# Revit family: NBS_ConceptCubicleSystems_PnlCbclSym_Curve
name_source: partatom
category: Specialty Equipment
units: mm (PartAtom-declared; Revit-internal decimal feet)

## family parameters
Always vertical = Yes
Cut with Voids When Loaded = No
Part Type = Normal
Room Calculation Point = No
Round Connector Dimension = Use Diameter
Shared = No
Work Plane-Based = No

## types (8) — shared parameters
AssetType = Fixed
Category = Ss_25_12_60_60:Panel cubicle systems
Description = Curve cubicles
DoorLeafMaterial = NBS_ConceptCubicleSystems_Z016_ZesteDeCitron-Yellow
DoorLeafUndercut = 150 mm
DurationUnit = year
Features = Black core with a radiused edge, back to back pull handle supplied with outward opening doors, non standard dimensions available on request, vandel and water resistant compact grade laminate
FittingMaterial = NBS_ConceptCubicleSystems_SatinAnodisedAluminium
Fittings = Powder coated aluminium with elliptical aluminium pilasters
IfcExportAs = IfcFurnitureType
IfcExportType = USERDEFINED
IsBuiltIn = Yes
ManufacturerName = Concept Cubicle Systems
ManufacturerURL = www.conceptcubiclesystems.co.uk
Material = Compact Grade Laminate
ModelReference = Curve Cubicles
NBSCertification = www.nationalbimlibrary.com/cert/b3h0bzth
NBSDescription = Panel cubicle system
NBSReference = 25-05-60/160
PanelSupports = 150 mm
PanelThickness = 13 mm
Panels = 12 mm Compact Grade Laminate
PartitionMaterial = NBS_ConceptCubicleSystems_Z016_ZesteDeCitron-Yellow
PartitionUndercut = 150 mm
PilasterMaterial = NBS_ConceptCubicleSystems_SatinAnodisedAluminium
ProductInformation = https://www.conceptcubiclesystems.co.uk
Size = 1500 x 1980 mm
Status = UNSET
Style = Cubicle
SystemManufacturer = Concept Cubicle Systems
Uniclass2015Code = Ss_25_12_60_60
Uniclass2015Title = Panel cubicle systems
Uniclass2015Version = Systems v1.17
Version = 3
WarrantyDurationUnit = year

## per-type parameters (varying)
| type | BIMObjectName | HasPartitionLeft | HasPartitionRight | HasPilasterLeftCorner | HasPilasterLeftWall | HasPilasterRight | HasPilasterRightCorner | HasPilasterRightWall | IsEndCubicle | IsFirstCubicle | IsMiddleCubicle | IsSingleCubicle | IsWallEndEndCubicle | IsWallEndFirstCubicle | IsWallEndSingleCubicle | IsWallToWallSingleCubicle | Name |
| SingleCubicle | NBS_ConceptCubicleSystems_PanelCubicleSystem_Curve_SingleCubicle | Yes | Yes | Yes | No | No | Yes | No | No | No | No | Yes | No | No | No | No | PanelCubicleSystem_Curve_SingleCubicle_ConceptCubicleSystems |
| WallToWallSingleCubicle | NBS_ConceptCubicleSystems_PanelCubicleSystem_Curve_WallToWallSingleCubicle | No | No | No | Yes | No | No | Yes | No | No | No | No | No | No | No | Yes | PanelCubicleSystem_Curve_WallToWallSingleCubicle_ConceptCubicleSystems |
| EndCubicle | NBS_ConceptCubicleSystems_PanelCubicleSystem_Curve_EndCubicle | No | Yes | No | No | No | Yes | No | Yes | No | No | No | No | No | No | No | PanelCubicleSystem_Curve_EndCubicle_ConceptCubicleSystems |
| FirstCubicle | NBS_ConceptCubicleSystems_PanelCubicleSystem_Curve_FirstCubicle | Yes | Yes | Yes | No | Yes | No | No | No | Yes | No | No | No | No | No | No | PanelCubicleSystem_Curve_FirstCubicle_ConceptCubicleSystems |
| WallEndFirstCubicle | NBS_ConceptCubicleSystems_PanelCubicleSystem_Curve_WallEndFirstCubicle | No | Yes | No | Yes | Yes | No | No | No | No | No | No | No | Yes | No | No | PanelCubicleSystem_Curve_WallEndFirstCubicle_ConceptCubicleSystems |
| WallEndSingleCubicle | NBS_ConceptCubicleSystems_PanelCubicleSystem_Curve_WallEndSingleCubicle | No | Yes | No | Yes | No | Yes | No | No | No | No | No | No | No | Yes | No | PanelCubicleSystem_Curve_WallEndSingleCubicle_ConceptCubicleSystems |
| MiddleCubicle | NBS_ConceptCubicleSystems_PanelCubicleSystem_Curve_MiddleCubicle | No | Yes | No | No | Yes | No | No | No | No | Yes | No | No | No | No | No | PanelCubicleSystem_Curve_MiddleCubicle_ConceptCubicleSystems |
| WallEndEndCubicle | NBS_ConceptCubicleSystems_PanelCubicleSystem_Curve_WallEndEndCubicle | No | No | No | No | No | No | Yes | No | No | No | No | Yes | No | No | No | PanelCubicleSystem_Curve_WallEndEndCubicle_ConceptCubicleSystems |

## geometry (parser evidence)
native form markers: Sweep x7
no freeform markers — native parametric forms only
